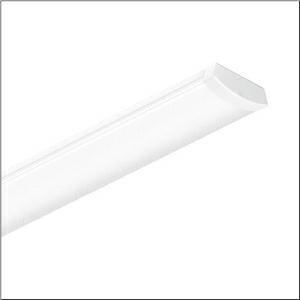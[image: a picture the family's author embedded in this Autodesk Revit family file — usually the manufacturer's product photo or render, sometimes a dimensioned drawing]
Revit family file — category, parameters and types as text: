
# Revit family: siluette_r__21_51ln12mkm40a3g_b368
name_source: partatom
category: Lighting Fixtures
units: mm (PartAtom-declared; Revit-internal decimal feet)

## family parameters
Cut with Voids When Loaded = No
Host = Face
Light Source = No
Part Type = Normal
Room Calculation Point = No
Round Connector Dimension = Use Diameter
Shared = No

## types (1)
- --- (1 x LED, 2980 lm, 20.6 W, 5000K)
    Apparent Load = 21 VA
    CIE Flux Codes = 43 73 92 94 100
    Color Rendering = 80
    Color Temperature = 5000K
    Default Elevation = 1800 mm
    Description = Siluette® 21, office luminaire, primary optical cover: enclosure, of PC, frosted, light emission: direct distribution, primary light characteristic: symmetric, installation type: suspended mounting, surface-mounted, LED, rated luminous flux: 5.010lm, luminous efficacy: 136lm/W, light colour: 830/840/850, colour temperature: 3000/4000/5000K, control gear: ON/OFF Multilumen, with terminal, 4-pole, mains connection: 220..240V, AC, 50/60Hz, rated input power: 37W, control gear: single battery element, housing, of sheet steel, white, length: 1.200mm, width: 152mm, height: 53mm, end cap, of PMMA, white, protection rating (complete): IP44, insulation class (complete): insulation class I (protective earthing), certification: CE, UKCA, protection symbol: D, impact resistance: IK04, permissible operating ambient temperature: +5..+40°C, standard: EN 60598-2-22, contact your sales advisor before using the luminaires in applications with unclear chemical exposure, large temperature fluctuations or condensation-forming humidity, corresponds to IFS (International Featured Standards) requirements for safety and quality in the food industry, packaging unit: 1 piece
    Height = 52 mm  [stored 0.170604 ft]
    Lamp = 1 x LED
    Lamp Light Flux = 2980 lm
    Lamp Power = 20.6 W
    Lamp count = 1
    Length = 1185 mm
    Luminous efficacy = 145 lm/W
    Manufacturer = Siteco
    ModVariant = No
    Model = 51LN12MKM40A3G
    Mounting Place = Ceiling
    Mounting Type = Pendant
    Number of Poles = 1
    OnlyDefault = Yes
    Power Factor = 1
    Product Name = Siluette® 21
    Product group = office luminaire | ceiling pendant
    ProductGroupID = 903
    Protection Class = Protection class I
    Protection Degree = IP 44
    RLX_Detail_Level = 1
    RLX_Emergency_Light_Flux = 0 lm
    RLX_Emergency_Type = 0
    RLX_Emergency_Type_DB = No
    RlxData = <blob elided: 19549 chars, md5=deccfb63>
    Socket = socket
    Standby Power = 0 W
    System Light Flux = 2980 lm
    System Power = 21 W
    Type Comments = individual setting: colour temperature 5000K, luminous flux: 60 % | (OFF | OFF | ON) | 200 mA
    Type Image = l_1296910.jpg
    URL = http://relux.com
    VarID = @adj_079527
    Voltage = 0 V
    Weight = 0.00 kg
    Width = 152 mm

note: [stored X ft] marks values corroborated as IEEE doubles in the binary element streams (Revit-internal decimal feet)

## geometry (parser evidence)
native form markers: Blend x4, Sweep x13
no freeform markers — native parametric forms only
